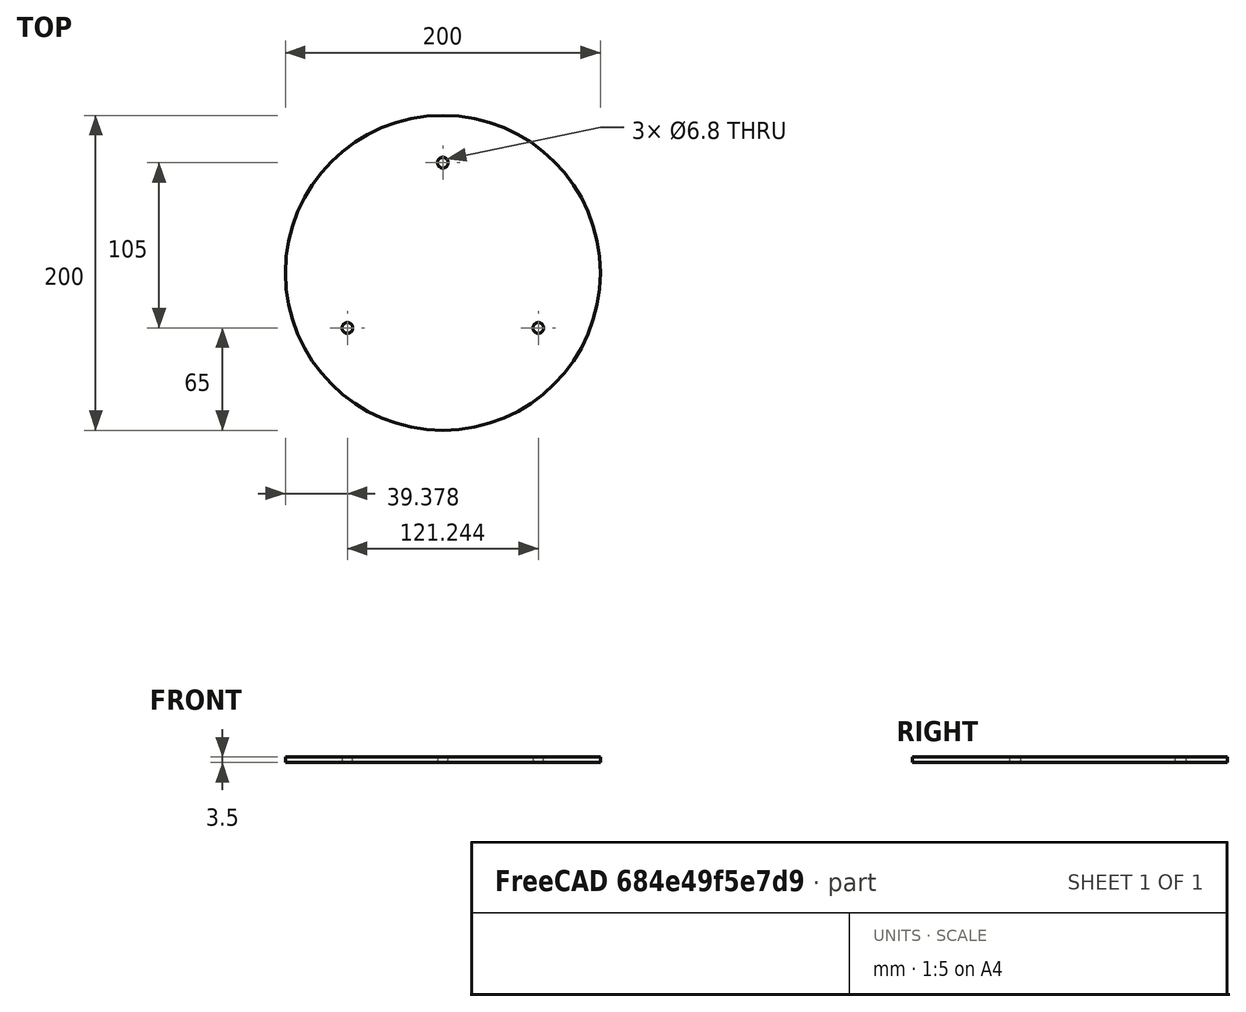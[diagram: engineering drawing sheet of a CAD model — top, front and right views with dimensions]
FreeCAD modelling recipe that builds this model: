
FCSTD DOCUMENT  (FreeCAD 0.17R13522 (Git))
Label: platte
License: All rights reserved
LicenseURL: http://en.wikipedia.org/wiki/All_rights_reserved
objects: Sketcher::SketchObject×1, PartDesign::Pad×1, PartDesign::Body×1
note: 4 computed .brp shape members not serialized (recipe doc carries the construction recipe); baked Part::Feature solids carry a one-line shape summary decoded from their .brp

FEATURE [Sketcher::SketchObject] Sketch
  MapMode = 5
  Support = -> [XY_Plane]
  sketch-geometry (10):
    g0: Circle CenterX=0 CenterY=0 CenterZ=0 NormalX=0 NormalY=0 NormalZ=1 AngleXU=0 Radius=100
    g1: GeomPoint X=0 Y=70 Z=0
    g2: Circle CenterX=0 CenterY=70 CenterZ=0 NormalX=0 NormalY=0 NormalZ=1 AngleXU=0 Radius=3.4
    g3: Circle CenterX=60.6218 CenterY=-35 CenterZ=0 NormalX=0 NormalY=0 NormalZ=1 AngleXU=0 Radius=3.4
    g4: Circle CenterX=-60.6218 CenterY=-35 CenterZ=0 NormalX=0 NormalY=0 NormalZ=1 AngleXU=0 Radius=3.4
    g5: LineSegment [constr] StartX=0 StartY=70 StartZ=0 EndX=60.6218 EndY=-35 EndZ=0
    g6: LineSegment [constr] StartX=0 StartY=70 StartZ=0 EndX=-60.6218 EndY=-35 EndZ=0
    g7: LineSegment [constr] StartX=-60.6218 StartY=-35 StartZ=0 EndX=60.6218 EndY=-35 EndZ=0
    g8: LineSegment [constr] StartX=0 StartY=70 StartZ=0 EndX=0 EndY=0 EndZ=0
    g9: LineSegment [constr] StartX=-60.6218 StartY=-35 StartZ=0 EndX=0 EndY=0 EndZ=0
  constraints (22):
    c: Coincident(g0,g-1)
    c: Radius(g0) = 100
    c: Coincident(g2,g1)
    c: Equal(g2,g3)
    c: Equal(g3,g4)
    c: Coincident(g5,g1)
    c: Coincident(g5,g3)
    c: Coincident(g6,g1)
    c: Coincident(g6,g4)
    c: Coincident(g7,g4)
    c: Coincident(g7,g3)
    c: Horizontal(g7)
    c: Equal(g6,g7)
    c: Equal(g7,g5)
    c: Coincident(g8,g1)
    c: Coincident(g8,g-1)
    c: Vertical(g8)
    c: Coincident(g9,g4)
    c: Coincident(g9,g-1)
    c: Equal(g8,g9)
    c: Radius(g3) = 3.4
    c: Distance(g-1,g3) = 70
FEATURE [PartDesign::Pad] Pad
  Length = 3.5
  Length2 = 100
  Profile = -> Sketch
  Type = 0
FEATURE [PartDesign::Body] Body
  Group = -> [Sketch,Pad]
  Origin = -> Origin
  Tip = -> Pad
